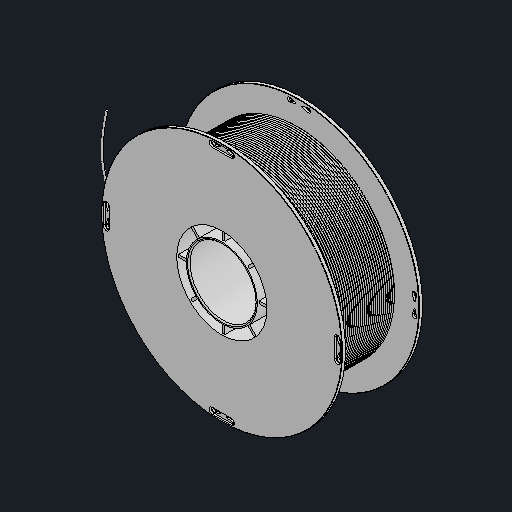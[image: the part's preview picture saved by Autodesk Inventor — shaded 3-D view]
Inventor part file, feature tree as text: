
AUTODESK INVENTOR PART (.ipt)
format: ipt  version: 2024.2 (Build 282272000, 272)  size: 2,681,344 bytes
history: native  units: mm
features: other x3, sweep x2, mirror x1
ambient origin geometry x8: Origin, YZ Plane, XZ Plane, XY Plane, X Axis, Y Axis, Z Axis, Center Point
bodies: Body1 (feature_tree), Body2 (feature_tree), Body3 (feature_tree)
feature tree (6):
  other  "솔리드1"
  other  "솔리드2"
  other  "솔리드3"
  mirror  "Mirror7"
  sweep  "Sweep1"
  sweep  "Sweep3"
